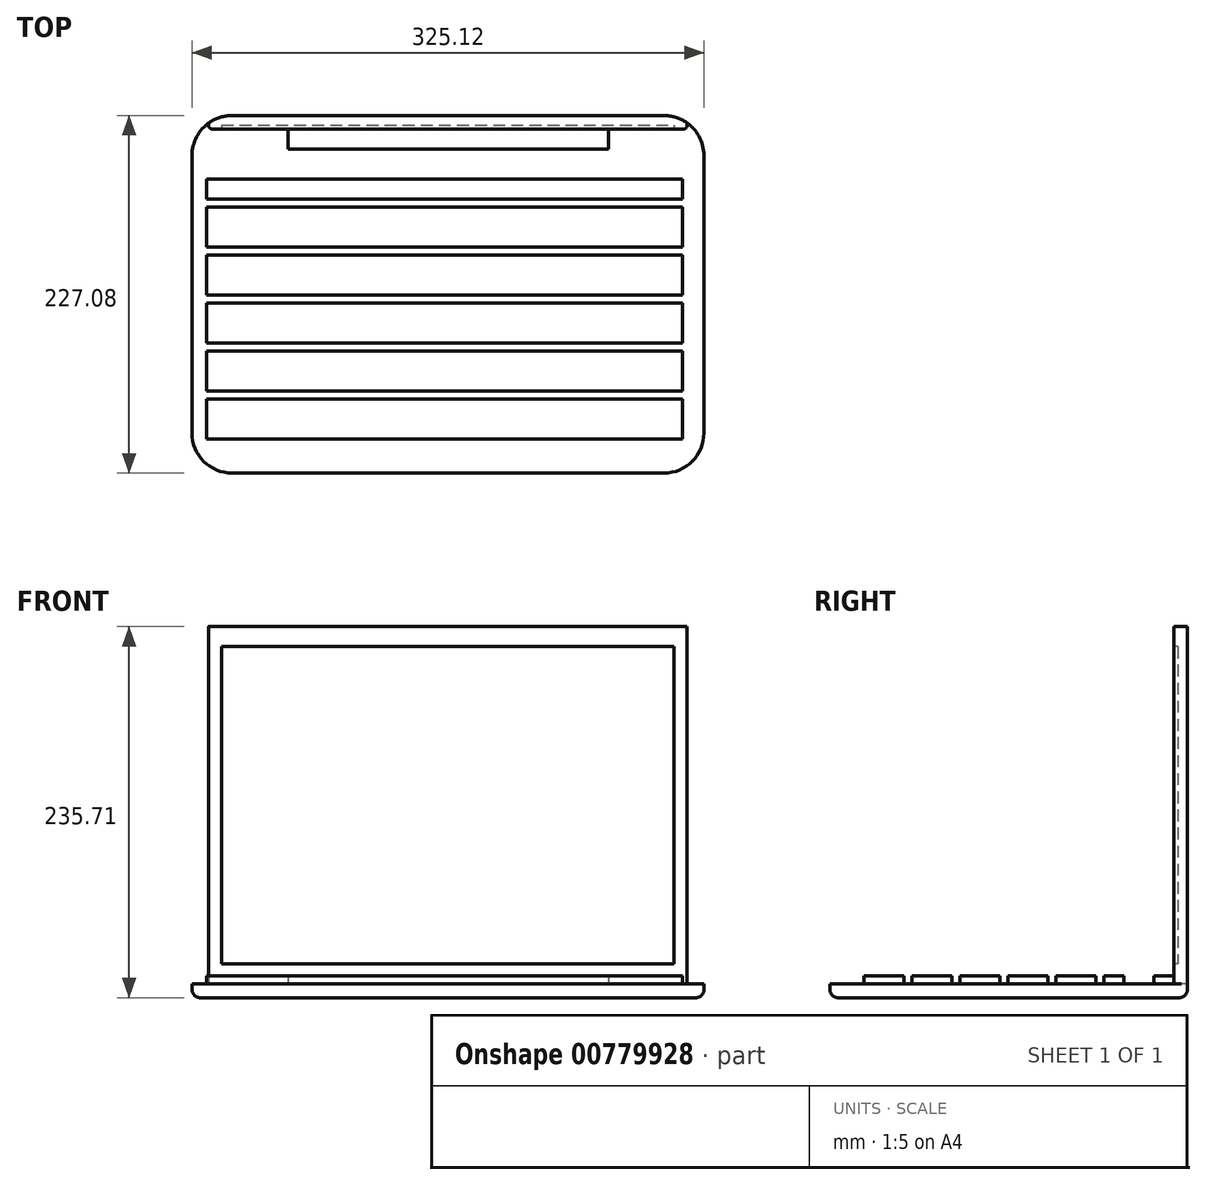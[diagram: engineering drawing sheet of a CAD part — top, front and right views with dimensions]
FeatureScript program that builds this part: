
annotation { "Feature Type Name" : "Feature", "Feature Type Description" : "" }
export const myFeature = defineFeature(function(context is Context, id is Id, definition is map)
    precondition{}
    {
        {
            var Q0;
            Q0=qCreatedBy(makeId("Top.planeOp"),FACE);
            var sketch = newSketch(context, id + "F0", { "sketchPlane" : qUnion([Q0])});
            skLineSegment(sketch, "E0.bottom", {"start": v(-134.84, 104.18) * mm, "end": v(139.48, 104.18) * mm});
            skLineSegment(sketch, "E0.top", {"start": v(-134.84, -122.9) * mm, "end": v(139.48, -122.9) * mm});
            skLineSegment(sketch, "E0.left", {"start": v(-160.24, 78.78) * mm, "end": v(-160.24, -97.5) * mm});
            skLineSegment(sketch, "E0.right", {"start": v(164.88, 78.78) * mm, "end": v(164.88, -97.5) * mm});
            skPoint(sketch, "E1.visualSharp", {"position": v(-160.24, 104.18) * mm});
            skArc(sketch, "E1.filletArc", {"start": v(-134.84, 104.18) * mm, "mid": v(-152.8, 96.74) * mm, "end": v(-160.24, 78.78) * mm});
            skPoint(sketch, "E2.visualSharp", {"position": v(164.88, 104.18) * mm});
            skArc(sketch, "E2.filletArc", {"start": v(164.88, 78.78) * mm, "mid": v(157.44, 96.74) * mm, "end": v(139.48, 104.18) * mm});
            skPoint(sketch, "E3.visualSharp", {"position": v(164.88, -122.9) * mm});
            skArc(sketch, "E3.filletArc", {"start": v(139.48, -122.9) * mm, "mid": v(157.44, -115.46) * mm, "end": v(164.88, -97.5) * mm});
            skPoint(sketch, "E4.visualSharp", {"position": v(-160.24, -122.9) * mm});
            skArc(sketch, "E4.filletArc", {"start": v(-160.24, -97.5) * mm, "mid": v(-152.8, -115.46) * mm, "end": v(-134.84, -122.9) * mm});
            skSolve(sketch);
        }
        {
            var Q0;
            Q0 = qSketchRegion(id + "F0", true);
            extrude(context, id + "F1", {"entities" : qUnion([Q0]), "depth" : 8.64 * mm, "offsetDistance" : 25.4 * mm});
        }
        {
            var Q0;
            Q0=makeQuery(id+"F1.opExtrude","CAP_FACE",FACE,{"disambiguationData":[OSD([sQuery(id+"F0.wireOp",EDGE,"E0.bottom"),sQuery(id+"F0.wireOp",EDGE,"E0.top"),sQuery(id+"F0.wireOp",EDGE,"E0.left"),sQuery(id+"F0.wireOp",EDGE,"E0.right"),sQuery(id+"F0.wireOp",EDGE,"E1.filletArc"),sQuery(id+"F0.wireOp",EDGE,"E2.filletArc"),sQuery(id+"F0.wireOp",EDGE,"E3.filletArc"),sQuery(id+"F0.wireOp",EDGE,"E4.filletArc")])],"isStart":false});
            var sketch = newSketch(context, id + "F2", { "sketchPlane" : qUnion([Q0])});
            skPoint(sketch, "E5.end.orphan", {"position": v(-99.28, 104.18) * mm});
            skPoint(sketch, "E5.start.orphan", {"position": v(2.32, 104.18) * mm});
            skPoint(sketch, "E6.MirrorCS.end.orphan", {"position": v(103.92, 104.18) * mm});
            skLineSegment(sketch, "E7", {"start": v(-80.61, 95.54) * mm, "end": v(-80.61, 104.18) * mm});
            skPoint(sketch, "E8.start.orphan", {"position": v(104.22, 91.48) * mm});
            skPoint(sketch, "E9.end.orphan", {"position": v(-99.28, 91.48) * mm});
            skLineSegment(sketch, "E10", {"start": v(-80.61, 95.54) * mm, "end": v(-99.28, 95.54) * mm});
            skLineSegment(sketch, "E11", {"start": v(-99.28, 95.54) * mm, "end": v(-99.28, 82.84) * mm});
            skLineSegment(sketch, "E12", {"start": v(-80.61, 95.54) * mm, "end": v(104.22, 95.54) * mm});
            skLineSegment(sketch, "E13", {"start": v(-99.28, 82.84) * mm, "end": v(104.22, 82.84) * mm});
            skLineSegment(sketch, "E14", {"start": v(104.22, 82.84) * mm, "end": v(104.22, 95.54) * mm});
            skSolve(sketch);
        }
        {
            var Q0;
            Q0 = qSketchRegion(id + "F2", true);
            extrude(context, id + "F3", {"entities" : qUnion([Q0]), "operationType" : NewBodyOperationType.ADD, "depth" : 5.08 * mm, "offsetDistance" : 25.4 * mm});
        }
        {
            var Q0;
            Q0=makeQuery(id+"F1.opExtrude","CAP_FACE",FACE,{"disambiguationData":[OSD([sQuery(id+"F0.wireOp",EDGE,"E0.bottom"),sQuery(id+"F0.wireOp",EDGE,"E0.top"),sQuery(id+"F0.wireOp",EDGE,"E0.left"),sQuery(id+"F0.wireOp",EDGE,"E0.right"),sQuery(id+"F0.wireOp",EDGE,"E1.filletArc"),sQuery(id+"F0.wireOp",EDGE,"E2.filletArc"),sQuery(id+"F0.wireOp",EDGE,"E3.filletArc"),sQuery(id+"F0.wireOp",EDGE,"E4.filletArc")])],"isStart":false});
            var sketch = newSketch(context, id + "F4", { "sketchPlane" : qUnion([Q0])});
            skLineSegment(sketch, "E15", {"start": v(-99.28, 95.54) * mm, "end": v(-99.28, 104.18) * mm});
            skLineSegment(sketch, "E16", {"start": v(104.22, 95.54) * mm, "end": v(104.22, 104.18) * mm});
            skLineSegment(sketch, "E17", {"start": v(104.22, 104.18) * mm, "end": v(-99.28, 104.18) * mm});
            skLineSegment(sketch, "E18", {"start": v(-99.28, 95.54) * mm, "end": v(104.22, 95.54) * mm});
            skLineSegment(sketch, "E19", {"start": v(104.22, 95.54) * mm, "end": v(158.56, 95.54) * mm});
            skLineSegment(sketch, "E20", {"start": v(139.48, 104.18) * mm, "end": v(104.22, 104.18) * mm});
            skLineSegment(sketch, "E21", {"start": v(-99.28, 104.18) * mm, "end": v(-134.84, 104.18) * mm});
            skLineSegment(sketch, "E22", {"start": v(-99.28, 95.54) * mm, "end": v(-154.1, 95.54) * mm});
            skPoint(sketch, "E22.endSnap0", {"position": v(-160.24, 93.51) * mm});
            skPoint(sketch, "E23.orphan", {"position": v(-160.24, 82.84) * mm});
            skArc(sketch, "E24", {"start": v(-134.84, 104.18) * mm, "mid": v(-145.4, 101.92) * mm, "end": v(-154.1, 95.54) * mm});
            skPoint(sketch, "E25.orphan", {"position": v(-160.24, 95.54) * mm});
            skPoint(sketch, "E26.orphan", {"position": v(-160.24, 104.18) * mm});
            skArc(sketch, "E27", {"start": v(158.56, 95.54) * mm, "mid": v(149.95, 101.92) * mm, "end": v(139.48, 104.18) * mm});
            skPoint(sketch, "E28.start.orphan", {"position": v(164.88, 95.54) * mm});
            skPoint(sketch, "E29.orphan", {"position": v(164.88, 104.18) * mm});
            skSolve(sketch);
        }
        {
            var Q0;
            Q0 = qSketchRegion(id + "F4", true);
            extrude(context, id + "F5", {"entities" : qUnion([Q0]), "operationType" : NewBodyOperationType.ADD, "depth" : 227.08 * mm, "offsetDistance" : 25.4 * mm});
        }
        {
            var Q0;
            Q0=makeQuery(id+"F5.opExtrude","SWEPT_FACE",FACE,{"disambiguationData":[OSD([sQuery(id+"F4.wireOp",EDGE,"E18"),sQuery(id+"F4.wireOp",EDGE,"E19"),sQuery(id+"F4.wireOp",EDGE,"E22")])]});
            var sketch = newSketch(context, id + "F6", { "sketchPlane" : qUnion([Q0])});
            skLineSegment(sketch, "E30.bottom", {"start": v(-141.4, 223.01) * mm, "end": v(145.86, 223.01) * mm});
            skLineSegment(sketch, "E30.top", {"start": v(-141.4, 21.34) * mm, "end": v(145.86, 21.34) * mm});
            skLineSegment(sketch, "E30.left", {"start": v(-141.4, 223.01) * mm, "end": v(-141.4, 21.34) * mm});
            skLineSegment(sketch, "E30.right", {"start": v(145.86, 223.01) * mm, "end": v(145.86, 21.34) * mm});
            skSolve(sketch);
        }
        {
            var Q0;
            Q0 = qSketchRegion(id + "F6", true);
            extrude(context, id + "F7", {"entities" : qUnion([Q0]), "operationType" : NewBodyOperationType.REMOVE, "oppositeDirection" : true, "depth" : 2.54 * mm, "offsetDistance" : 25.4 * mm});
        }
        {
            var Q0;
            Q0=makeQuery(id+"F1.opExtrude","CAP_FACE",FACE,{"disambiguationData":[OSD([sQuery(id+"F0.wireOp",EDGE,"E0.bottom"),sQuery(id+"F0.wireOp",EDGE,"E0.top"),sQuery(id+"F0.wireOp",EDGE,"E0.left"),sQuery(id+"F0.wireOp",EDGE,"E0.right"),sQuery(id+"F0.wireOp",EDGE,"E1.filletArc"),sQuery(id+"F0.wireOp",EDGE,"E2.filletArc"),sQuery(id+"F0.wireOp",EDGE,"E3.filletArc"),sQuery(id+"F0.wireOp",EDGE,"E4.filletArc")])],"isStart":false});
            var sketch = newSketch(context, id + "F8", { "sketchPlane" : qUnion([Q0])});
            skLineSegment(sketch, "E31.bottom", {"start": v(151.13, -106.45) * mm, "end": v(-151.13, -106.45) * mm});
            skLineSegment(sketch, "E31.top", {"start": v(151.13, 63.73) * mm, "end": v(-151.13, 63.73) * mm});
            skLineSegment(sketch, "E31.left", {"start": v(151.13, -106.45) * mm, "end": v(151.13, 63.73) * mm});
            skLineSegment(sketch, "E31.right", {"start": v(-151.13, -106.45) * mm, "end": v(-151.13, 63.73) * mm});
            skPoint(sketch, "E31.middle", {"position": v(0, -21.36) * mm});
            skLineSegment(sketch, "E32", {"start": v(-151.13, 51.03) * mm, "end": v(151.13, 51.03) * mm});
            skLineSegment(sketch, "E33", {"start": v(-151.13, 20.55) * mm, "end": v(151.13, 20.55) * mm});
            skLineSegment(sketch, "E34", {"start": v(-151.13, -9.93) * mm, "end": v(151.13, -9.93) * mm});
            skLineSegment(sketch, "E35", {"start": v(-151.13, -40.41) * mm, "end": v(151.13, -40.41) * mm});
            skLineSegment(sketch, "E36", {"start": v(-151.13, -70.9) * mm, "end": v(151.13, -70.9) * mm});
            skLineSegment(sketch, "E37", {"start": v(-151.13, -101.37) * mm, "end": v(151.13, -101.37) * mm});
            skLineSegment(sketch, "E38", {"start": v(-151.13, 45.95) * mm, "end": v(151.13, 45.95) * mm});
            skLineSegment(sketch, "E39", {"start": v(-151.13, 15.47) * mm, "end": v(151.13, 15.47) * mm});
            skLineSegment(sketch, "E40", {"start": v(-151.13, -15.01) * mm, "end": v(151.13, -15.01) * mm});
            skLineSegment(sketch, "E41", {"start": v(-151.13, -45.5) * mm, "end": v(151.13, -45.5) * mm});
            skLineSegment(sketch, "E42", {"start": v(-151.13, -75.97) * mm, "end": v(151.13, -75.97) * mm});
            skLineSegment(sketch, "E43", {"start": v(-133.35, 63.73) * mm, "end": v(-133.35, -106.45) * mm});
            skLineSegment(sketch, "E44", {"start": v(-115.57, 63.73) * mm, "end": v(-115.57, -106.45) * mm});
            skLineSegment(sketch, "E45.MirrorCS", {"start": v(-97.79, 63.73) * mm, "end": v(-97.8, -106.45) * mm});
            skLineSegment(sketch, "E46.MirrorCS", {"start": v(-80, 63.73) * mm, "end": v(-80.01, -106.45) * mm});
            skLineSegment(sketch, "E47.MirrorCS", {"start": v(-62.23, 63.73) * mm, "end": v(-62.23, -106.45) * mm});
            skLineSegment(sketch, "E48.MirrorCS", {"start": v(-44.45, 63.73) * mm, "end": v(-44.45, -106.45) * mm});
            skLineSegment(sketch, "E49.MirrorCS", {"start": v(-26.67, 63.73) * mm, "end": v(-26.67, -106.45) * mm});
            skLineSegment(sketch, "E50.MirrorCS", {"start": v(-8.89, 63.73) * mm, "end": v(-8.9, -106.45) * mm});
            skLineSegment(sketch, "E51.MirrorCS", {"start": v(8.9, 63.73) * mm, "end": v(8.89, -106.45) * mm});
            skLineSegment(sketch, "E52.MirrorCS", {"start": v(26.67, 63.73) * mm, "end": v(26.67, -106.45) * mm});
            skLineSegment(sketch, "E53.MirrorCS", {"start": v(44.45, 63.73) * mm, "end": v(44.45, -106.45) * mm});
            skLineSegment(sketch, "E54.MirrorCS", {"start": v(62.23, 63.73) * mm, "end": v(62.23, -106.45) * mm});
            skLineSegment(sketch, "E55.MirrorCS", {"start": v(80.01, 63.73) * mm, "end": v(80, -106.45) * mm});
            skLineSegment(sketch, "E56.MirrorCS", {"start": v(97.8, 63.73) * mm, "end": v(97.79, -106.45) * mm});
            skLineSegment(sketch, "E57.MirrorCS", {"start": v(115.57, 63.73) * mm, "end": v(115.57, -106.45) * mm});
            skLineSegment(sketch, "E58.MirrorCS", {"start": v(133.35, 63.73) * mm, "end": v(133.35, -106.45) * mm});
            skLineSegment(sketch, "E59", {"start": v(-137.16, 63.73) * mm, "end": v(-137.16, -106.45) * mm});
            skLineSegment(sketch, "E60", {"start": v(-119.38, 63.73) * mm, "end": v(-119.38, -106.45) * mm});
            skLineSegment(sketch, "E61", {"start": v(-101.6, -106.45) * mm, "end": v(-101.6, 63.73) * mm});
            skLineSegment(sketch, "E62", {"start": v(-83.82, -106.45) * mm, "end": v(-83.82, 63.73) * mm});
            skLineSegment(sketch, "E63", {"start": v(-66.04, -106.45) * mm, "end": v(-66.04, 63.73) * mm});
            skLineSegment(sketch, "E64", {"start": v(-48.26, -106.45) * mm, "end": v(-48.26, 63.73) * mm});
            skLineSegment(sketch, "E65", {"start": v(-30.48, -106.45) * mm, "end": v(-30.48, 63.73) * mm});
            skLineSegment(sketch, "E66", {"start": v(-14.49, 63.73) * mm, "end": v(-14.49, -106.45) * mm});
            skSolve(sketch);
        }
        {
            var Q0;
            {var subQ0=sQuery(id+"F8.wireOp",EDGE,"E31.top");Q0=makeQuery(id+"F8.imprint","IMPRINT",FACE,{"disambiguationData":[TD([[makeQuery(id+"F8.imprint","IMPRINT",EDGE,{"derivedFrom":subQ0}),1.0]])]});}
            var Q1;
            {var subQ0=sQuery(id+"F8.wireOp",EDGE,"E37");Q1=makeQuery(id+"F8.imprint","IMPRINT",FACE,{"disambiguationData":[TD([[makeQuery(id+"F8.imprint","IMPRINT",EDGE,{"derivedFrom":subQ0}),1.0]])]});}
            var Q2;
            {var subQ0=sQuery(id+"F8.wireOp",EDGE,"E36");Q2=makeQuery(id+"F8.imprint","IMPRINT",FACE,{"disambiguationData":[TD([[makeQuery(id+"F8.imprint","IMPRINT",EDGE,{"derivedFrom":subQ0}),1.0]])]});}
            var Q3;
            {var subQ0=sQuery(id+"F8.wireOp",EDGE,"E35");Q3=makeQuery(id+"F8.imprint","IMPRINT",FACE,{"disambiguationData":[TD([[makeQuery(id+"F8.imprint","IMPRINT",EDGE,{"derivedFrom":subQ0}),1.0]])]});}
            var Q4;
            {var subQ0=sQuery(id+"F8.wireOp",EDGE,"E34");Q4=makeQuery(id+"F8.imprint","IMPRINT",FACE,{"disambiguationData":[TD([[makeQuery(id+"F8.imprint","IMPRINT",EDGE,{"derivedFrom":subQ0}),1.0]])]});}
            var Q5;
            {var subQ0=sQuery(id+"F8.wireOp",EDGE,"E33");Q5=makeQuery(id+"F8.imprint","IMPRINT",FACE,{"disambiguationData":[TD([[makeQuery(id+"F8.imprint","IMPRINT",EDGE,{"derivedFrom":subQ0}),1.0]])]});}
            extrude(context, id + "F9", {"entities" : qUnion([Q0, Q1, Q2, Q3, Q4, Q5]), "operationType" : NewBodyOperationType.ADD, "depth" : 5.08 * mm, "offsetDistance" : 25.4 * mm});
        }
        {
            var Q0;
            Q0=makeQuery(id+"F1.opExtrude","CAP_EDGE",EDGE,{"disambiguationData":[OSD([sQuery(id+"F0.wireOp",EDGE,"E0.bottom")])],"isStart":true});
            fillet(context, id + "F10", {"entities" : qUnion([Q0]), "tangentPropagation" : true, "radius" : 5.08 * mm, "defaultsChanged" : false, "vertexSettings" : [], "allowEdgeOverflow" : false});
        }
        {
            var Q0;
            Q0=makeQuery(id+"F5.opExtrude","SWEPT_EDGE",EDGE,{"disambiguationData":[OSD([sQuery(id+"F4.wireOp",EDGE,"E22"),sQuery(id+"F4.wireOp",EDGE,"E24")])]});
            var Q1;
            Q1=makeQuery(id+"F5.opExtrude","SWEPT_EDGE",EDGE,{"disambiguationData":[OSD([sQuery(id+"F0.wireOp",EDGE,"E2.filletArc"),sQuery(id+"F4.wireOp",EDGE,"E19"),sQuery(id+"F4.wireOp",EDGE,"E27")])]});
            fillet(context, id + "F11", {"entities" : qUnion([Q0, Q1]), "tangentPropagation" : true, "radius" : 2.54 * mm, "defaultsChanged" : true, "vertexSettings" : [], "allowEdgeOverflow" : false});
        }
    });
